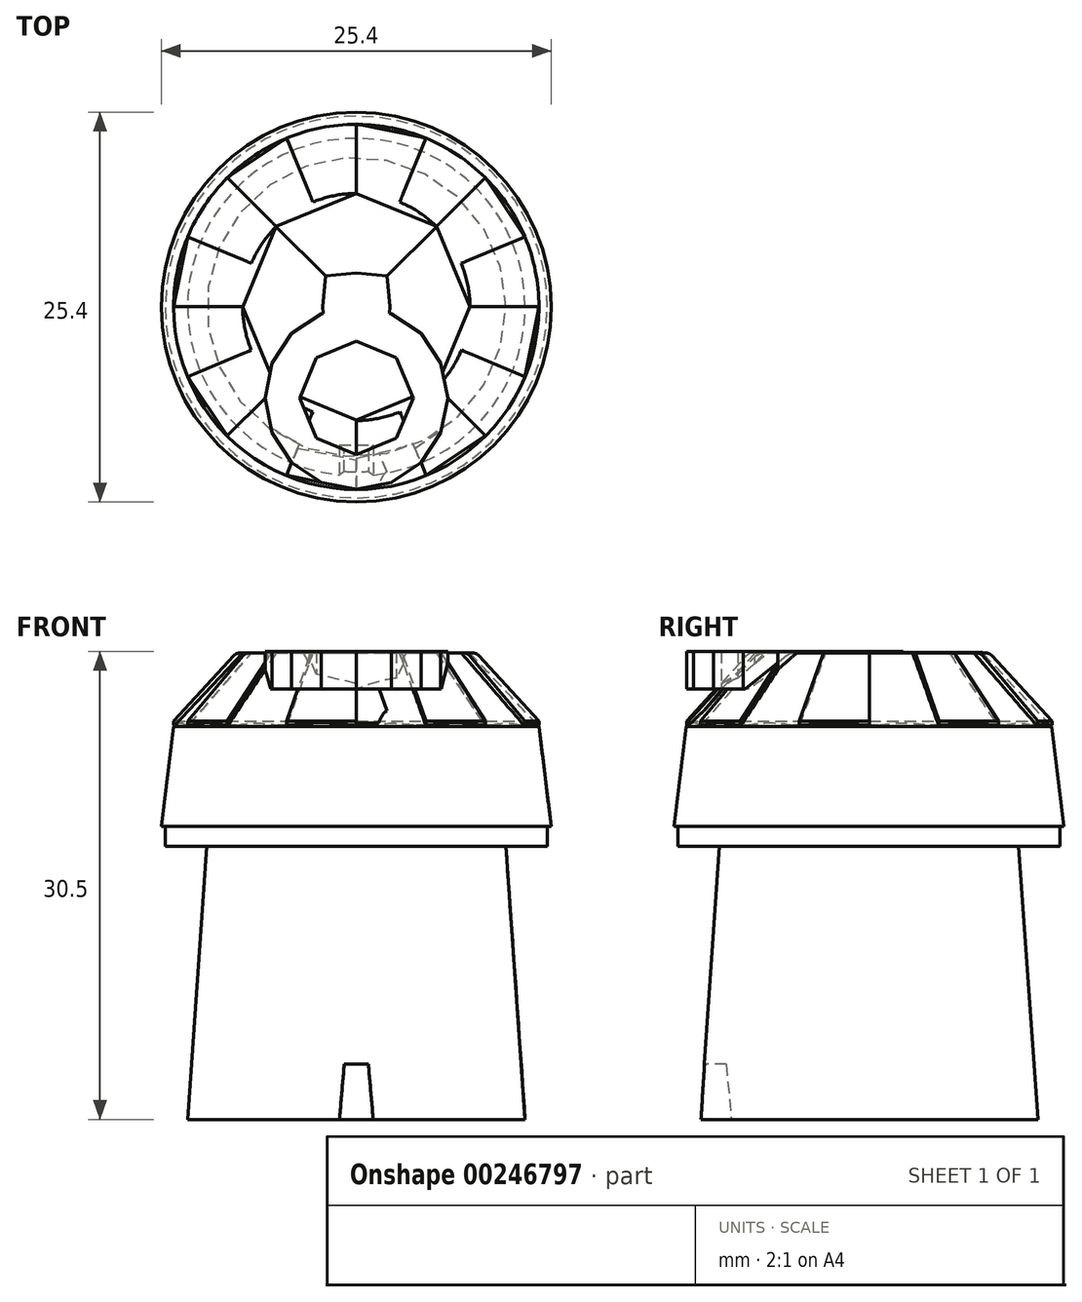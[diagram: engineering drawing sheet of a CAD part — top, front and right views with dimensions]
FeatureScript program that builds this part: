
annotation { "Feature Type Name" : "Feature", "Feature Type Description" : "" }
export const myFeature = defineFeature(function(context is Context, id is Id, definition is map)
    precondition{}
    {
        {
            var Q0;
            Q0=qCreatedBy(makeId("Front.planeOp"),FACE);
            var sketch = newSketch(context, id + "F0", { "sketchPlane" : qUnion([Q0])});
            skLineSegment(sketch, "E0", {"start": v(0, 0) * mm, "end": v(5.5, 0) * mm});
            skLineSegment(sketch, "E1", {"start": v(0, 8.9) * mm, "end": v(4.87, 8.9) * mm});
            skLineSegment(sketch, "E2", {"start": v(4.87, 8.9) * mm, "end": v(5.5, 0) * mm});
            skLineSegment(sketch, "E3", {"start": v(4.87, 8.9) * mm, "end": v(6.22, 8.9) * mm});
            skLineSegment(sketch, "E4", {"start": v(6.22, 8.9) * mm, "end": v(6.22, 9.55) * mm});
            skLineSegment(sketch, "E5", {"start": v(6.22, 9.55) * mm, "end": v(6.35, 9.55) * mm});
            skLineSegment(sketch, "E6", {"start": v(0, 0) * mm, "end": v(0, 15.2) * mm});
            skLineSegment(sketch, "E7", {"start": v(11.32, 12.8) * mm, "end": v(-3.84, 12.8) * mm, "construction": true});
            skLineSegment(sketch, "E8", {"start": v(5.95, 12.8) * mm, "end": v(6.35, 9.55) * mm});
            skLineSegment(sketch, "E9", {"start": v(15.11, 15.2) * mm, "end": v(0, 15.2) * mm, "construction": true});
            skLineSegment(sketch, "E10", {"start": v(0, 15.2) * mm, "end": v(3.7, 15.2) * mm});
            skLineSegment(sketch, "E11", {"start": v(3.7, 15.2) * mm, "end": v(5.95, 12.8) * mm});
            skSolve(sketch);
        }
        {
            var Q0;
            Q0=qSketchRegion(id+"F0",true);
            extrude(context, id + "F1", {"entities" : qUnion([Q0]), "depth" : 0.01 * mm});
        }
        {
            var Q0;
            Q0=makeQuery(id+"F1.opExtrude","CAP_FACE",FACE,{"disambiguationData":[OSD([sQuery(id+"F0.wireOp",EDGE,"E0"),sQuery(id+"F0.wireOp",EDGE,"E2"),sQuery(id+"F0.wireOp",EDGE,"E3"),sQuery(id+"F0.wireOp",EDGE,"E4"),sQuery(id+"F0.wireOp",EDGE,"E5"),sQuery(id+"F0.wireOp",EDGE,"sixM9Us5-RhuG-cWRY-0vQ0-8mJEDSYx7DVo"),sQuery(id+"F0.wireOp",EDGE,"EqexqkoD-ppkq-6j4X-MFRW-SI8jGCcGb6jM"),sQuery(id+"F0.wireOp",EDGE,"g6Ss7R6n-PE6a-QBEk-j47J-OcREIYiym4vq"),sQuery(id+"F0.wireOp",EDGE,"74306cc8-111f-4a76-b4a3-b401b2c3296c0.MirrorCS"),sQuery(id+"F0.wireOp",EDGE,"74306cc8-111f-4a76-b4a3-b401b2c3296c2.MirrorCS"),sQuery(id+"F0.wireOp",EDGE,"74306cc8-111f-4a76-b4a3-b401b2c3296c3.MirrorCS"),sQuery(id+"F0.wireOp",EDGE,"74306cc8-111f-4a76-b4a3-b401b2c3296c6.MirrorCS"),sQuery(id+"F0.wireOp",EDGE,"74306cc8-111f-4a76-b4a3-b401b2c3296c7.MirrorCS"),sQuery(id+"F0.wireOp",EDGE,"74306cc8-111f-4a76-b4a3-b401b2c3296c9.MirrorCS"),sQuery(id+"F0.wireOp",EDGE,"74306cc8-111f-4a76-b4a3-b401b2c3296c13.MirrorCS")])],"isStart":false});
            var Q1;
            Q1=makeQuery(id+"F1.opExtrude","CAP_EDGE",EDGE,{"disambiguationData":[OSD([sQuery(id+"F0.wireOp",EDGE,"E6")])],"isStart":false});
            revolve(context, id + "F2", {"operationType" : NewBodyOperationType.ADD, "entities" : qUnion([Q0]), "axis" : qUnion([Q1]), "revolveType" : RevolveType.FULL});
        }
        {
            var Q0;
            {var subQ0=sQuery(id+"F0.wireOp",EDGE,"E0");Q0=makeQuery(id+"F2.boolean.opBoolean","MERGE",FACE,{"derivedFrom":[makeQuery(id+"F1.opExtrude","SWEPT_FACE",FACE,{"disambiguationData":[OSD([subQ0])]}),makeQuery(id+"F2.opRevolve","SWEPT_FACE",FACE,{"disambiguationData":[OSD([subQ0])]})]});}
            var sketch = newSketch(context, id + "F3", { "sketchPlane" : qUnion([Q0])});
            skCircle(sketch, "E12", {"center": v(0, 0) * mm, "radius": 6 * mm, "construction": true});
            skLineSegment(sketch, "E13", {"start": v(0, 6) * mm, "end": v(0, 4.5) * mm, "construction": true});
            skLineSegment(sketch, "E14", {"start": v(0, 4.5) * mm, "end": v(0.55, 4.5) * mm});
            skLineSegment(sketch, "E15", {"start": v(0.55, 4.5) * mm, "end": v(0.55, 5.97) * mm});
            skLineSegment(sketch, "E16", {"start": v(0, 4.5) * mm, "end": v(-0.55, 4.5) * mm});
            skLineSegment(sketch, "E17", {"start": v(-0.55, 4.5) * mm, "end": v(-0.55, 5.97) * mm});
            skLineSegment(sketch, "E18", {"start": v(-0.55, 5.97) * mm, "end": v(0.55, 5.97) * mm});
            skSolve(sketch);
        }
        {
            var Q0;
            Q0=qSketchRegion(id+"F3",true);
            extrude(context, id + "F4", {"entities" : qUnion([Q0]), "operationType" : NewBodyOperationType.REMOVE, "oppositeDirection" : true, "depth" : 1.8 * mm});
        }
        {
            var Q0;
            Q0=makeQuery(id+"F4.boolean.opBoolean","COPY",EDGE,{"derivedFrom":makeQuery(id+"F4.opExtrude","CAP_EDGE",EDGE,{"disambiguationData":[OSD([sQuery(id+"F3.wireOp",EDGE,"E17")])],"isStart":false})});
            var Q1;
            Q1=makeQuery(id+"F4.boolean.opBoolean","COPY",EDGE,{"derivedFrom":makeQuery(id+"F4.opExtrude","CAP_EDGE",EDGE,{"disambiguationData":[OSD([sQuery(id+"F3.wireOp",EDGE,"E15")])],"isStart":false})});
            var Q2;
            Q2=makeQuery(id+"F4.boolean.opBoolean","COPY",EDGE,{"derivedFrom":makeQuery(id+"F4.opExtrude","CAP_EDGE",EDGE,{"disambiguationData":[OSD([sQuery(id+"F3.wireOp",EDGE,"E14"),sQuery(id+"F3.wireOp",EDGE,"E16")])],"isStart":false})});
            chamfer(context, id + "F5", {"entities" : qUnion([Q0, Q1, Q2]), "chamferType" : ChamferType.OFFSET_ANGLE, "width" : 1.8 * mm, "oppositeDirection" : false, "angle" : 5 * degree, "tangentPropagation" : true});
        }
        {
            var Q0;
            {var subQ0=sQuery(id+"F0.wireOp",EDGE,"E10");Q0=makeQuery(id+"F2.boolean.opBoolean","MERGE",FACE,{"derivedFrom":[makeQuery(id+"F1.opExtrude","SWEPT_FACE",FACE,{"disambiguationData":[OSD([subQ0])]}),makeQuery(id+"F2.opRevolve","SWEPT_FACE",FACE,{"disambiguationData":[OSD([subQ0])]})]});}
            var sketch = newSketch(context, id + "F6", { "sketchPlane" : qUnion([Q0])});
            skLineSegment(sketch, "E19.bottom", {"start": v(1, -1) * mm, "end": v(-1, -1) * mm, "construction": true});
            skLineSegment(sketch, "E19.top", {"start": v(1, 1) * mm, "end": v(-1, 1) * mm, "construction": true});
            skLineSegment(sketch, "E19.left", {"start": v(1, -1) * mm, "end": v(1, 1) * mm, "construction": true});
            skLineSegment(sketch, "E19.right", {"start": v(-1, -1) * mm, "end": v(-1, 1) * mm, "construction": true});
            skPoint(sketch, "E19.middle", {"position": v(0, 0) * mm});
            skLineSegment(sketch, "E20", {"start": v(0, 0) * mm, "end": v(1.1, 0) * mm, "construction": true});
            skPoint(sketch, "E20.endSnap0", {"position": v(1, 0) * mm});
            skLineSegment(sketch, "E21", {"start": v(0, 0) * mm, "end": v(0, 1.1) * mm, "construction": true});
            skPoint(sketch, "E21.endSnap0", {"position": v(0, 1) * mm});
            skLineSegment(sketch, "E22", {"start": v(0, 0) * mm, "end": v(-1.1, 0) * mm, "construction": true});
            skLineSegment(sketch, "E23", {"start": v(0, 0) * mm, "end": v(0, -1.1) * mm, "construction": true});
            skPoint(sketch, "E23.endSnap0", {"position": v(0, -1) * mm});
            skLineSegment(sketch, "E24", {"start": v(1, 1) * mm, "end": v(1.1, 0) * mm});
            skLineSegment(sketch, "E25", {"start": v(1, -1) * mm, "end": v(1.1, 0) * mm});
            skLineSegment(sketch, "E26", {"start": v(0, 1.1) * mm, "end": v(1, 1) * mm});
            skLineSegment(sketch, "E27", {"start": v(0, 1.1) * mm, "end": v(-1, 1) * mm});
            skLineSegment(sketch, "E28", {"start": v(-1, 1) * mm, "end": v(-1.1, 0) * mm});
            skLineSegment(sketch, "E29", {"start": v(-1, -1) * mm, "end": v(-1.1, 0) * mm});
            skLineSegment(sketch, "E30", {"start": v(-1, -1) * mm, "end": v(0, -1.1) * mm});
            skLineSegment(sketch, "E31", {"start": v(1, -1) * mm, "end": v(0, -1.1) * mm});
            skCircle(sketch, "E32", {"center": v(0, 0) * mm, "radius": 3.7 * mm, "construction": true});
            skLineSegment(sketch, "E33", {"start": v(0, -1.1) * mm, "end": v(0, -3.7) * mm, "construction": true});
            skLineSegment(sketch, "E34.bottom", {"start": v(2.62, -2.62) * mm, "end": v(-2.62, -2.62) * mm, "construction": true});
            skLineSegment(sketch, "E34.top", {"start": v(2.62, 2.62) * mm, "end": v(-2.62, 2.62) * mm, "construction": true});
            skLineSegment(sketch, "E34.left", {"start": v(2.62, -2.62) * mm, "end": v(2.62, 2.62) * mm, "construction": true});
            skLineSegment(sketch, "E34.right", {"start": v(-2.62, -2.62) * mm, "end": v(-2.62, 2.62) * mm, "construction": true});
            skLineSegment(sketch, "E35", {"start": v(-2.62, 2.62) * mm, "end": v(-1, 1) * mm});
            skLineSegment(sketch, "E36", {"start": v(-1, -1) * mm, "end": v(-2.62, -2.62) * mm});
            skLineSegment(sketch, "E37", {"start": v(1, -1) * mm, "end": v(2.62, -2.62) * mm});
            skLineSegment(sketch, "E38", {"start": v(1, 1) * mm, "end": v(2.62, 2.62) * mm});
            skLineSegment(sketch, "E39", {"start": v(-2.62, 2.62) * mm, "end": v(0, 3.69) * mm});
            skLineSegment(sketch, "E40", {"start": v(0, 3.69) * mm, "end": v(2.62, 2.62) * mm});
            skLineSegment(sketch, "E41", {"start": v(2.62, 2.62) * mm, "end": v(3.7, 0) * mm});
            skLineSegment(sketch, "E42", {"start": v(3.7, 0) * mm, "end": v(2.62, -2.62) * mm});
            skLineSegment(sketch, "E43", {"start": v(2.62, -2.62) * mm, "end": v(0, -3.7) * mm});
            skLineSegment(sketch, "E44", {"start": v(-2.62, -2.62) * mm, "end": v(0, -3.7) * mm});
            skLineSegment(sketch, "E45", {"start": v(-2.62, -2.62) * mm, "end": v(-3.7, 0) * mm});
            skLineSegment(sketch, "E46", {"start": v(-3.7, 0) * mm, "end": v(-2.62, 2.62) * mm});
            skSolve(sketch);
        }
        {
            var Q0;
            Q0=makeQuery(id+"F6.imprint","IMPRINT",FACE,{"disambiguationData":[TD([[makeQuery(id+"F6.imprint","IMPRINT",EDGE,{"derivedFrom":sQuery(id+"F6.wireOp",EDGE,"E24")}),-1.0]])]});
            extrude(context, id + "F7", {"entities" : qUnion([Q0]), "operationType" : NewBodyOperationType.ADD, "depth" : 0.05 * mm});
        }
        {
            var Q0;
            {var subQ1=sQuery(id+"F6.wireOp",EDGE,"E28");Q0=makeQuery(id+"F6.imprint","IMPRINT",FACE,{"disambiguationData":[TD([[makeQuery(id+"F6.imprint","IMPRINT",EDGE,{"derivedFrom":subQ1}),-1.0]])]});}
            var Q1;
            {var subQ1=sQuery(id+"F6.wireOp",EDGE,"E24");Q1=makeQuery(id+"F6.imprint","IMPRINT",FACE,{"disambiguationData":[TD([[makeQuery(id+"F6.imprint","IMPRINT",EDGE,{"derivedFrom":subQ1}),1.0]])]});}
            extrude(context, id + "F8", {"entities" : qUnion([Q0, Q1]), "operationType" : NewBodyOperationType.ADD, "depth" : 0.01 * mm});
        }
        {
            var Q0;
            Q0=makeQuery(id+"F6.imprint","IMPRINT",FACE,{"disambiguationData":[TD([[makeQuery(id+"F6.imprint","IMPRINT",EDGE,{"derivedFrom":sQuery(id+"F6.wireOp",EDGE,"E30")}),-1.0]])]});
            var Q1;
            {var subQ5=sQuery(id+"F6.wireOp",EDGE,"E26");Q1=makeQuery(id+"F6.imprint","IMPRINT",FACE,{"disambiguationData":[TD([[makeQuery(id+"F6.imprint","IMPRINT",EDGE,{"derivedFrom":subQ5}),1.0]])]});}
            extrude(context, id + "F9", {"entities" : qUnion([Q0, Q1]), "operationType" : NewBodyOperationType.ADD, "depth" : 0.02 * mm});
        }
        {
            var Q0;
            Q0=qCreatedBy(makeId("Top.planeOp"),FACE);
            cPlane(context, id + "F10", {"entities" : qUnion([Q0]), "cplaneType" : CPlaneType.OFFSET, "offset" : 15.2 * mm, "width" : 150 * mm, "height" : 150 * mm});
        }
        {
            var Q0;
            Q0=qCreatedBy(id+"F10.planeOp",FACE);
            var sketch = newSketch(context, id + "F11", { "sketchPlane" : qUnion([Q0])});
            skLineSegment(sketch, "E47", {"start": v(0, -5.95) * mm, "end": v(0, -3.7) * mm});
            skLineSegment(sketch, "E48", {"start": v(1.3, -3.16) * mm, "end": v(2.28, -5.5) * mm});
            skLineSegment(sketch, "E49.1.0", {"start": v(4.2, -4.2) * mm, "end": v(2.62, -2.62) * mm});
            skLineSegment(sketch, "E49.1.1", {"start": v(3.16, -1.3) * mm, "end": v(5.5, -2.28) * mm});
            skLineSegment(sketch, "E49.2.0", {"start": v(5.95, 0) * mm, "end": v(3.7, 0) * mm});
            skLineSegment(sketch, "E49.2.1", {"start": v(3.16, 1.3) * mm, "end": v(5.5, 2.28) * mm});
            skPoint(sketch, "E49.center", {"position": v(0, 0) * mm});
            skLineSegment(sketch, "E50.1.3.0", {"start": v(4.2, 4.2) * mm, "end": v(2.62, 2.62) * mm});
            skLineSegment(sketch, "E50.3.3.0", {"start": v(1.3, 3.16) * mm, "end": v(2.28, 5.5) * mm});
            skLineSegment(sketch, "E50.1.4.0", {"start": v(0, 5.95) * mm, "end": v(0, 3.7) * mm});
            skLineSegment(sketch, "E50.3.4.0", {"start": v(-1.3, 3.16) * mm, "end": v(-2.28, 5.5) * mm});
            skLineSegment(sketch, "E50.1.5.0", {"start": v(-4.2, 4.2) * mm, "end": v(-2.62, 2.62) * mm});
            skLineSegment(sketch, "E50.3.5.0", {"start": v(-3.16, 1.3) * mm, "end": v(-5.5, 2.28) * mm});
            skLineSegment(sketch, "E50.1.6.0", {"start": v(-5.95, 0) * mm, "end": v(-3.7, 0) * mm});
            skLineSegment(sketch, "E50.3.6.0", {"start": v(-3.16, -1.3) * mm, "end": v(-5.5, -2.28) * mm});
            skLineSegment(sketch, "E50.1.7.0", {"start": v(-4.2, -4.2) * mm, "end": v(-2.62, -2.62) * mm});
            skLineSegment(sketch, "E50.3.7.0", {"start": v(-1.3, -3.16) * mm, "end": v(-2.28, -5.5) * mm});
            skLineSegment(sketch, "E51", {"start": v(0, -3.7) * mm, "end": v(1.3, -3.16) * mm});
            skLineSegment(sketch, "E52", {"start": v(1.3, -3.16) * mm, "end": v(2.62, -2.62) * mm});
            skLineSegment(sketch, "E53", {"start": v(2.62, -2.62) * mm, "end": v(3.16, -1.3) * mm});
            skLineSegment(sketch, "E54", {"start": v(3.16, -1.3) * mm, "end": v(3.7, 0) * mm});
            skLineSegment(sketch, "E55", {"start": v(3.7, 0) * mm, "end": v(3.16, 1.3) * mm});
            skLineSegment(sketch, "E56", {"start": v(3.16, 1.3) * mm, "end": v(2.62, 2.62) * mm});
            skLineSegment(sketch, "E57", {"start": v(2.62, 2.62) * mm, "end": v(1.3, 3.16) * mm});
            skLineSegment(sketch, "E58", {"start": v(1.3, 3.16) * mm, "end": v(0, 3.7) * mm});
            skLineSegment(sketch, "E59", {"start": v(0, 3.7) * mm, "end": v(-1.3, 3.16) * mm});
            skLineSegment(sketch, "E60", {"start": v(-1.3, 3.16) * mm, "end": v(-2.62, 2.62) * mm});
            skLineSegment(sketch, "E61", {"start": v(-2.62, 2.62) * mm, "end": v(-3.16, 1.3) * mm});
            skLineSegment(sketch, "E62", {"start": v(-3.16, 1.3) * mm, "end": v(-3.7, 0) * mm});
            skLineSegment(sketch, "E63", {"start": v(-3.7, 0) * mm, "end": v(-3.16, -1.3) * mm});
            skLineSegment(sketch, "E64", {"start": v(-3.16, -1.3) * mm, "end": v(-2.62, -2.62) * mm});
            skLineSegment(sketch, "E65", {"start": v(-2.62, -2.62) * mm, "end": v(-1.3, -3.16) * mm});
            skLineSegment(sketch, "E66", {"start": v(-1.3, -3.16) * mm, "end": v(0, -3.7) * mm});
            skLineSegment(sketch, "E67", {"start": v(-2.28, -5.5) * mm, "end": v(0, -5.95) * mm});
            skLineSegment(sketch, "E68", {"start": v(0, -5.95) * mm, "end": v(2.28, -5.5) * mm});
            skLineSegment(sketch, "E69", {"start": v(2.28, -5.5) * mm, "end": v(4.2, -4.2) * mm});
            skLineSegment(sketch, "E70", {"start": v(4.2, -4.2) * mm, "end": v(5.5, -2.28) * mm});
            skLineSegment(sketch, "E71", {"start": v(5.5, -2.28) * mm, "end": v(5.95, 0) * mm});
            skLineSegment(sketch, "E72", {"start": v(5.95, 0) * mm, "end": v(5.5, 2.28) * mm});
            skLineSegment(sketch, "E73", {"start": v(5.5, 2.28) * mm, "end": v(4.2, 4.2) * mm});
            skLineSegment(sketch, "E74", {"start": v(4.2, 4.2) * mm, "end": v(2.28, 5.5) * mm});
            skLineSegment(sketch, "E75", {"start": v(2.28, 5.5) * mm, "end": v(0, 5.95) * mm});
            skLineSegment(sketch, "E76", {"start": v(0, 5.95) * mm, "end": v(-2.28, 5.5) * mm});
            skLineSegment(sketch, "E77", {"start": v(-2.28, 5.5) * mm, "end": v(-4.2, 4.2) * mm});
            skLineSegment(sketch, "E78", {"start": v(-4.2, 4.2) * mm, "end": v(-5.5, 2.28) * mm});
            skLineSegment(sketch, "E79", {"start": v(-5.5, 2.28) * mm, "end": v(-5.95, 0) * mm});
            skLineSegment(sketch, "E80", {"start": v(-5.95, 0) * mm, "end": v(-5.5, -2.28) * mm});
            skLineSegment(sketch, "E81", {"start": v(-5.5, -2.28) * mm, "end": v(-4.2, -4.2) * mm});
            skLineSegment(sketch, "E82", {"start": v(-4.2, -4.2) * mm, "end": v(-2.28, -5.5) * mm});
            skSolve(sketch);
        }
        {
            var Q0;
            Q0=makeQuery(id+"F11.imprint","IMPRINT",FACE,{"disambiguationData":[TD([[makeQuery(id+"F11.imprint","IMPRINT",EDGE,{"derivedFrom":sQuery(id+"F11.wireOp",EDGE,"E47")}),1.0]])]});
            var Q1;
            Q1=makeQuery(id+"F11.imprint","IMPRINT",FACE,{"disambiguationData":[TD([[makeQuery(id+"F11.imprint","IMPRINT",EDGE,{"derivedFrom":sQuery(id+"F11.wireOp",EDGE,"E48")}),1.0]])]});
            var Q2;
            Q2=makeQuery(id+"F11.imprint","IMPRINT",FACE,{"disambiguationData":[TD([[makeQuery(id+"F11.imprint","IMPRINT",EDGE,{"derivedFrom":sQuery(id+"F11.wireOp",EDGE,"E49.1.1")}),1.0]])]});
            var Q3;
            Q3=makeQuery(id+"F11.imprint","IMPRINT",FACE,{"disambiguationData":[TD([[makeQuery(id+"F11.imprint","IMPRINT",EDGE,{"derivedFrom":sQuery(id+"F11.wireOp",EDGE,"E49.2.1")}),1.0]])]});
            var Q4;
            Q4=makeQuery(id+"F11.imprint","IMPRINT",FACE,{"disambiguationData":[TD([[makeQuery(id+"F11.imprint","IMPRINT",EDGE,{"derivedFrom":sQuery(id+"F11.wireOp",EDGE,"E50.3.3.0")}),1.0]])]});
            var Q5;
            Q5=makeQuery(id+"F11.imprint","IMPRINT",FACE,{"disambiguationData":[TD([[makeQuery(id+"F11.imprint","IMPRINT",EDGE,{"derivedFrom":sQuery(id+"F11.wireOp",EDGE,"E50.3.4.0")}),1.0]])]});
            var Q6;
            Q6=makeQuery(id+"F11.imprint","IMPRINT",FACE,{"disambiguationData":[TD([[makeQuery(id+"F11.imprint","IMPRINT",EDGE,{"derivedFrom":sQuery(id+"F11.wireOp",EDGE,"E50.3.5.0")}),1.0]])]});
            var Q7;
            Q7=makeQuery(id+"F11.imprint","IMPRINT",FACE,{"disambiguationData":[TD([[makeQuery(id+"F11.imprint","IMPRINT",EDGE,{"derivedFrom":sQuery(id+"F11.wireOp",EDGE,"E50.3.6.0")}),1.0]])]});
            var Q8;
            Q8=makeQuery(id+"F1.opExtrude","SWEPT_BODY",BODY,{"disambiguationData":[OSD([sQuery(id+"F0.wireOp",EDGE,"E0"),sQuery(id+"F0.wireOp",EDGE,"E2"),sQuery(id+"F0.wireOp",EDGE,"E3"),sQuery(id+"F0.wireOp",EDGE,"E4"),sQuery(id+"F0.wireOp",EDGE,"E5"),sQuery(id+"F0.wireOp",EDGE,"E6"),sQuery(id+"F0.wireOp",EDGE,"E8"),sQuery(id+"F0.wireOp",EDGE,"E10"),sQuery(id+"F0.wireOp",EDGE,"E11")])]});
            extrude(context, id + "F12", {"entities" : qUnion([Q0, Q1, Q2, Q3, Q4, Q5, Q6, Q7]), "operationType" : NewBodyOperationType.ADD, "oppositeDirection" : true, "endBoundEntityBody" : qUnion([Q8]), "depth" : 2.35 * mm});
        }
        {
            var Q0;
            Q0=makeQuery(id+"F12.opExtrude","CAP_EDGE",EDGE,{"disambiguationData":[OSD([sQuery(id+"F11.wireOp",EDGE,"E67")])],"isStart":true});
            var Q1;
            Q1=makeQuery(id+"F12.opExtrude","CAP_EDGE",EDGE,{"disambiguationData":[OSD([sQuery(id+"F11.wireOp",EDGE,"E69")])],"isStart":true});
            var Q2;
            Q2=makeQuery(id+"F12.opExtrude","CAP_EDGE",EDGE,{"disambiguationData":[OSD([sQuery(id+"F11.wireOp",EDGE,"E71")])],"isStart":true});
            var Q3;
            Q3=makeQuery(id+"F12.opExtrude","CAP_EDGE",EDGE,{"disambiguationData":[OSD([sQuery(id+"F11.wireOp",EDGE,"E73")])],"isStart":true});
            var Q4;
            Q4=makeQuery(id+"F12.opExtrude","CAP_EDGE",EDGE,{"disambiguationData":[OSD([sQuery(id+"F11.wireOp",EDGE,"E75")])],"isStart":true});
            var Q5;
            Q5=makeQuery(id+"F12.opExtrude","CAP_EDGE",EDGE,{"disambiguationData":[OSD([sQuery(id+"F11.wireOp",EDGE,"E77")])],"isStart":true});
            var Q6;
            Q6=makeQuery(id+"F12.opExtrude","CAP_EDGE",EDGE,{"disambiguationData":[OSD([sQuery(id+"F11.wireOp",EDGE,"E79")])],"isStart":true});
            var Q7;
            Q7=makeQuery(id+"F12.opExtrude","CAP_EDGE",EDGE,{"disambiguationData":[OSD([sQuery(id+"F11.wireOp",EDGE,"E81")])],"isStart":true});
            chamfer(context, id + "F13", {"entities" : qUnion([Q0, Q1, Q2, Q3, Q4, Q5, Q6, Q7]), "chamferType" : ChamferType.OFFSET_ANGLE, "width" : 2 * mm, "oppositeDirection" : false, "angle" : 48 * degree, "tangentPropagation" : true});
        }
        {
            var Q0;
            Q0=makeQuery(id+"F11.imprint","IMPRINT",FACE,{"disambiguationData":[TD([[makeQuery(id+"F11.imprint","IMPRINT",EDGE,{"derivedFrom":sQuery(id+"F11.wireOp",EDGE,"E47")}),-1.0]])]});
            var Q1;
            Q1=makeQuery(id+"F11.imprint","IMPRINT",FACE,{"disambiguationData":[TD([[makeQuery(id+"F11.imprint","IMPRINT",EDGE,{"derivedFrom":sQuery(id+"F11.wireOp",EDGE,"E49.1.0")}),-1.0]])]});
            var Q2;
            Q2=makeQuery(id+"F11.imprint","IMPRINT",FACE,{"disambiguationData":[TD([[makeQuery(id+"F11.imprint","IMPRINT",EDGE,{"derivedFrom":sQuery(id+"F11.wireOp",EDGE,"E49.2.0")}),-1.0]])]});
            var Q3;
            Q3=makeQuery(id+"F11.imprint","IMPRINT",FACE,{"disambiguationData":[TD([[makeQuery(id+"F11.imprint","IMPRINT",EDGE,{"derivedFrom":sQuery(id+"F11.wireOp",EDGE,"E50.1.3.0")}),-1.0]])]});
            var Q4;
            Q4=makeQuery(id+"F11.imprint","IMPRINT",FACE,{"disambiguationData":[TD([[makeQuery(id+"F11.imprint","IMPRINT",EDGE,{"derivedFrom":sQuery(id+"F11.wireOp",EDGE,"E50.1.4.0")}),-1.0]])]});
            var Q5;
            Q5=makeQuery(id+"F11.imprint","IMPRINT",FACE,{"disambiguationData":[TD([[makeQuery(id+"F11.imprint","IMPRINT",EDGE,{"derivedFrom":sQuery(id+"F11.wireOp",EDGE,"E50.1.5.0")}),-1.0]])]});
            var Q6;
            Q6=makeQuery(id+"F11.imprint","IMPRINT",FACE,{"disambiguationData":[TD([[makeQuery(id+"F11.imprint","IMPRINT",EDGE,{"derivedFrom":sQuery(id+"F11.wireOp",EDGE,"E50.1.6.0")}),-1.0]])]});
            var Q7;
            Q7=makeQuery(id+"F11.imprint","IMPRINT",FACE,{"disambiguationData":[TD([[makeQuery(id+"F11.imprint","IMPRINT",EDGE,{"derivedFrom":sQuery(id+"F11.wireOp",EDGE,"E50.1.7.0")}),-1.0]])]});
            extrude(context, id + "F14", {"entities" : qUnion([Q0, Q1, Q2, Q3, Q4, Q5, Q6, Q7]), "oppositeDirection" : true, "depth" : 2.45 * mm});
        }
        {
            var Q0;
            Q0=makeQuery(id+"F14.opExtrude","CAP_EDGE",EDGE,{"disambiguationData":[OSD([sQuery(id+"F11.wireOp",EDGE,"E82")])],"isStart":true});
            var Q1;
            Q1=makeQuery(id+"F14.opExtrude","CAP_EDGE",EDGE,{"disambiguationData":[OSD([sQuery(id+"F11.wireOp",EDGE,"E68")])],"isStart":true});
            var Q2;
            Q2=makeQuery(id+"F14.opExtrude","CAP_EDGE",EDGE,{"disambiguationData":[OSD([sQuery(id+"F11.wireOp",EDGE,"E70")])],"isStart":true});
            var Q3;
            Q3=makeQuery(id+"F14.opExtrude","CAP_EDGE",EDGE,{"disambiguationData":[OSD([sQuery(id+"F11.wireOp",EDGE,"E72")])],"isStart":true});
            var Q4;
            Q4=makeQuery(id+"F14.opExtrude","CAP_EDGE",EDGE,{"disambiguationData":[OSD([sQuery(id+"F11.wireOp",EDGE,"E74")])],"isStart":true});
            var Q5;
            Q5=makeQuery(id+"F14.opExtrude","CAP_EDGE",EDGE,{"disambiguationData":[OSD([sQuery(id+"F11.wireOp",EDGE,"E76")])],"isStart":true});
            var Q6;
            Q6=makeQuery(id+"F14.opExtrude","CAP_EDGE",EDGE,{"disambiguationData":[OSD([sQuery(id+"F11.wireOp",EDGE,"E78")])],"isStart":true});
            var Q7;
            Q7=makeQuery(id+"F14.opExtrude","CAP_EDGE",EDGE,{"disambiguationData":[OSD([sQuery(id+"F11.wireOp",EDGE,"E80")])],"isStart":true});
            chamfer(context, id + "F15", {"entities" : qUnion([Q0, Q1, Q2, Q3, Q4, Q5, Q6, Q7]), "chamferType" : ChamferType.OFFSET_ANGLE, "width" : 2 * mm, "oppositeDirection" : false, "angle" : 48 * degree, "tangentPropagation" : true});
        }
        {
            var Q0;
            Q0=makeQuery(id+"F1.opExtrude","SWEPT_BODY",BODY,{"disambiguationData":[OSD([sQuery(id+"F0.wireOp",EDGE,"E0"),sQuery(id+"F0.wireOp",EDGE,"E2"),sQuery(id+"F0.wireOp",EDGE,"E3"),sQuery(id+"F0.wireOp",EDGE,"E4"),sQuery(id+"F0.wireOp",EDGE,"E5"),sQuery(id+"F0.wireOp",EDGE,"E6"),sQuery(id+"F0.wireOp",EDGE,"E8"),sQuery(id+"F0.wireOp",EDGE,"E10"),sQuery(id+"F0.wireOp",EDGE,"E11")])]});
            var Q1;
            Q1=makeQuery(id+"F12.opExtrude","CAP_VERTEX",VERTEX,{"disambiguationData":[OSD([sQuery(id+"F11.wireOp",EDGE,"E47"),sQuery(id+"F11.wireOp",EDGE,"E67"),sQuery(id+"F11.wireOp",EDGE,"E68")])],"isStart":false});
            transform(context, id + "F16", {"entities" : qUnion([Q0]), "transformType" : TransformType.SCALE_UNIFORMLY, "scale" : 2, "scalePoint" : qUnion([Q1]), "makeCopy" : false});
        }
        {
            var Q0;
            {var subQ0=sQuery(id+"F11.wireOp",EDGE,"E79");var subQ1=sQuery(id+"F0.wireOp",EDGE,"E10");var subQ2=makeQuery(id+"F1.opExtrude","SWEPT_FACE",FACE,{"disambiguationData":[OSD([subQ1])]});var subQ3=sQuery(id+"F0.wireOp",EDGE,"E11");var subQ4=makeQuery(id+"F2.opRevolve","SWEPT_FACE",FACE,{"disambiguationData":[OSD([subQ1])]});var subQ5=sQuery(id+"F6.wireOp",EDGE,"E46");var subQ6=makeQuery(id+"F2.opRevolve","SWEPT_EDGE",EDGE,{"disambiguationData":[OSD([subQ1,subQ3])]});Q0=makeQuery(id+"F13.opChamfer","BLEND_EDGE",EDGE,{"blendedFrom":[makeQuery(id+"F12.opExtrude","CAP_EDGE",EDGE,{"disambiguationData":[OSD([subQ0])],"isStart":true}),makeQuery(id+"F12.boolean.opBoolean","MERGE",FACE,{"derivedFrom":[makeQuery(id+"F8.boolean.opBoolean","SPLIT",FACE,{"disambiguationData":[TD([subQ2,subQ4,makeQuery(id+"F2.opRevolve","SWEPT_FACE",FACE,{"disambiguationData":[OSD([subQ3])]}),makeQuery(id+"F8.opExtrude","SWEPT_FACE",FACE,{"disambiguationData":[OSD([sQuery(id+"F6.wireOp",EDGE,"E45")])]}),makeQuery(id+"F8.opExtrude","SWEPT_FACE",FACE,{"disambiguationData":[OSD([subQ5])]}),makeQuery(id+"F8.opExtrude","SWEPT_FACE",FACE,{"disambiguationData":[OSD([subQ1,subQ3]),TDD([makeQuery(id+"F6.imprint","IMPRINT",EDGE,{"disambiguationData":[TD([[makeQuery(id+"F6.imprint","INTERSECT",VERTEX,{"derivedFrom":[subQ6,subQ5]}),1.0]])],"derivedFrom":subQ6})])]})])],"derivedFrom":makeQuery(id+"F2.boolean.opBoolean","MERGE",FACE,{"derivedFrom":[subQ2,subQ4]})}),makeQuery(id+"F12.opExtrude","CAP_FACE",FACE,{"disambiguationData":[OSD([sQuery(id+"F11.wireOp",EDGE,"E50.3.5.0"),sQuery(id+"F11.wireOp",EDGE,"E50.1.6.0"),sQuery(id+"F11.wireOp",EDGE,"E62"),subQ0])],"isStart":true})]})],"blendedInto":[makeQuery(id+"F12.boolean.opBoolean","MERGE",FACE,{"derivedFrom":[makeQuery(id+"F8.boolean.opBoolean","SPLIT",FACE,{"disambiguationData":[TD([subQ2,subQ4,makeQuery(id+"F2.opRevolve","SWEPT_FACE",FACE,{"disambiguationData":[OSD([subQ3])]}),makeQuery(id+"F8.opExtrude","SWEPT_FACE",FACE,{"disambiguationData":[OSD([sQuery(id+"F6.wireOp",EDGE,"E45")])]}),makeQuery(id+"F8.opExtrude","SWEPT_FACE",FACE,{"disambiguationData":[OSD([subQ5])]}),makeQuery(id+"F8.opExtrude","SWEPT_FACE",FACE,{"disambiguationData":[OSD([subQ1,subQ3]),TDD([makeQuery(id+"F6.imprint","IMPRINT",EDGE,{"disambiguationData":[TD([[makeQuery(id+"F6.imprint","INTERSECT",VERTEX,{"derivedFrom":[subQ6,subQ5]}),1.0]])],"derivedFrom":subQ6})])]})])],"derivedFrom":makeQuery(id+"F2.boolean.opBoolean","MERGE",FACE,{"derivedFrom":[subQ2,subQ4]})}),makeQuery(id+"F12.opExtrude","CAP_FACE",FACE,{"disambiguationData":[OSD([sQuery(id+"F11.wireOp",EDGE,"E50.3.5.0"),sQuery(id+"F11.wireOp",EDGE,"E50.1.6.0"),sQuery(id+"F11.wireOp",EDGE,"E62"),subQ0])],"isStart":true})]})]});}
            var Q1;
            {var subQ0=sQuery(id+"F11.wireOp",EDGE,"E77");var subQ1=sQuery(id+"F6.wireOp",EDGE,"E39");var subQ2=sQuery(id+"F0.wireOp",EDGE,"E11");var subQ3=makeQuery(id+"F2.opRevolve","SWEPT_FACE",FACE,{"disambiguationData":[OSD([subQ2])]});var subQ4=sQuery(id+"F0.wireOp",EDGE,"E10");var subQ5=makeQuery(id+"F2.opRevolve","SWEPT_FACE",FACE,{"disambiguationData":[OSD([subQ4])]});var subQ6=makeQuery(id+"F1.opExtrude","SWEPT_FACE",FACE,{"disambiguationData":[OSD([subQ4])]});var subQ7=makeQuery(id+"F2.opRevolve","SWEPT_EDGE",EDGE,{"disambiguationData":[OSD([subQ4,subQ2])]});var subQ8=sQuery(id+"F6.wireOp",EDGE,"E35");var subQ10=sQuery(id+"F6.wireOp",EDGE,"E38");Q1=makeQuery(id+"F13.opChamfer","BLEND_EDGE",EDGE,{"blendedFrom":[makeQuery(id+"F12.opExtrude","CAP_EDGE",EDGE,{"disambiguationData":[OSD([subQ0])],"isStart":true}),makeQuery(id+"F12.boolean.opBoolean","MERGE",FACE,{"derivedFrom":[makeQuery(id+"F9.boolean.opBoolean","SPLIT",FACE,{"disambiguationData":[TD([makeQuery(id+"F9.opExtrude","SWEPT_FACE",FACE,{"disambiguationData":[OSD([subQ4,subQ2]),TDD([makeQuery(id+"F6.imprint","IMPRINT",EDGE,{"disambiguationData":[TD([[makeQuery(id+"F6.imprint","INTERSECT",VERTEX,{"derivedFrom":[subQ7,subQ1]}),-1.0]])],"derivedFrom":subQ7})])]})])],"derivedFrom":makeQuery(id+"F8.boolean.opBoolean","SPLIT",FACE,{"disambiguationData":[TD([subQ3,makeQuery(id+"F7.opExtrude","SWEPT_FACE",FACE,{"disambiguationData":[OSD([sQuery(id+"F6.wireOp",EDGE,"E26")])]}),makeQuery(id+"F7.opExtrude","SWEPT_FACE",FACE,{"disambiguationData":[OSD([sQuery(id+"F6.wireOp",EDGE,"E27")])]}),makeQuery(id+"F8.opExtrude","SWEPT_FACE",FACE,{"disambiguationData":[OSD([subQ8])]}),makeQuery(id+"F8.opExtrude","SWEPT_FACE",FACE,{"disambiguationData":[OSD([subQ10])]}),makeQuery(id+"F8.opExtrude","SWEPT_FACE",FACE,{"disambiguationData":[OSD([subQ4,subQ2]),TDD([makeQuery(id+"F6.imprint","IMPRINT",EDGE,{"disambiguationData":[TD([[makeQuery(id+"F6.imprint","INTERSECT",VERTEX,{"derivedFrom":[subQ7,sQuery(id+"F6.wireOp",EDGE,"E41")]}),-1.0]])],"derivedFrom":subQ7})])]}),makeQuery(id+"F8.opExtrude","SWEPT_FACE",FACE,{"disambiguationData":[OSD([subQ4,subQ2]),TDD([makeQuery(id+"F6.imprint","IMPRINT",EDGE,{"disambiguationData":[TD([[makeQuery(id+"F6.imprint","INTERSECT",VERTEX,{"derivedFrom":[subQ7,sQuery(id+"F6.wireOp",EDGE,"E46")]}),1.0]])],"derivedFrom":subQ7})])]})])],"derivedFrom":makeQuery(id+"F2.boolean.opBoolean","MERGE",FACE,{"derivedFrom":[subQ6,subQ5]})})}),makeQuery(id+"F12.opExtrude","CAP_FACE",FACE,{"disambiguationData":[OSD([sQuery(id+"F11.wireOp",EDGE,"E50.3.4.0"),sQuery(id+"F11.wireOp",EDGE,"E50.1.5.0"),sQuery(id+"F11.wireOp",EDGE,"E60"),subQ0])],"isStart":true})]})],"blendedInto":[makeQuery(id+"F12.boolean.opBoolean","MERGE",FACE,{"derivedFrom":[makeQuery(id+"F9.boolean.opBoolean","SPLIT",FACE,{"disambiguationData":[TD([makeQuery(id+"F9.opExtrude","SWEPT_FACE",FACE,{"disambiguationData":[OSD([subQ4,subQ2]),TDD([makeQuery(id+"F6.imprint","IMPRINT",EDGE,{"disambiguationData":[TD([[makeQuery(id+"F6.imprint","INTERSECT",VERTEX,{"derivedFrom":[subQ7,subQ1]}),-1.0]])],"derivedFrom":subQ7})])]})])],"derivedFrom":makeQuery(id+"F8.boolean.opBoolean","SPLIT",FACE,{"disambiguationData":[TD([subQ3,makeQuery(id+"F7.opExtrude","SWEPT_FACE",FACE,{"disambiguationData":[OSD([sQuery(id+"F6.wireOp",EDGE,"E26")])]}),makeQuery(id+"F7.opExtrude","SWEPT_FACE",FACE,{"disambiguationData":[OSD([sQuery(id+"F6.wireOp",EDGE,"E27")])]}),makeQuery(id+"F8.opExtrude","SWEPT_FACE",FACE,{"disambiguationData":[OSD([subQ8])]}),makeQuery(id+"F8.opExtrude","SWEPT_FACE",FACE,{"disambiguationData":[OSD([subQ10])]}),makeQuery(id+"F8.opExtrude","SWEPT_FACE",FACE,{"disambiguationData":[OSD([subQ4,subQ2]),TDD([makeQuery(id+"F6.imprint","IMPRINT",EDGE,{"disambiguationData":[TD([[makeQuery(id+"F6.imprint","INTERSECT",VERTEX,{"derivedFrom":[subQ7,sQuery(id+"F6.wireOp",EDGE,"E41")]}),-1.0]])],"derivedFrom":subQ7})])]}),makeQuery(id+"F8.opExtrude","SWEPT_FACE",FACE,{"disambiguationData":[OSD([subQ4,subQ2]),TDD([makeQuery(id+"F6.imprint","IMPRINT",EDGE,{"disambiguationData":[TD([[makeQuery(id+"F6.imprint","INTERSECT",VERTEX,{"derivedFrom":[subQ7,sQuery(id+"F6.wireOp",EDGE,"E46")]}),1.0]])],"derivedFrom":subQ7})])]})])],"derivedFrom":makeQuery(id+"F2.boolean.opBoolean","MERGE",FACE,{"derivedFrom":[subQ6,subQ5]})})}),makeQuery(id+"F12.opExtrude","CAP_FACE",FACE,{"disambiguationData":[OSD([sQuery(id+"F11.wireOp",EDGE,"E50.3.4.0"),sQuery(id+"F11.wireOp",EDGE,"E50.1.5.0"),sQuery(id+"F11.wireOp",EDGE,"E60"),subQ0])],"isStart":true})]})]});}
            var Q2;
            {var subQ0=sQuery(id+"F11.wireOp",EDGE,"E75");var subQ1=sQuery(id+"F0.wireOp",EDGE,"E11");var subQ2=makeQuery(id+"F2.opRevolve","SWEPT_FACE",FACE,{"disambiguationData":[OSD([subQ1])]});var subQ3=sQuery(id+"F0.wireOp",EDGE,"E10");var subQ4=makeQuery(id+"F2.opRevolve","SWEPT_FACE",FACE,{"disambiguationData":[OSD([subQ3])]});var subQ5=makeQuery(id+"F1.opExtrude","SWEPT_FACE",FACE,{"disambiguationData":[OSD([subQ3])]});var subQ6=sQuery(id+"F6.wireOp",EDGE,"E40");var subQ7=makeQuery(id+"F2.opRevolve","SWEPT_EDGE",EDGE,{"disambiguationData":[OSD([subQ3,subQ1])]});var subQ8=sQuery(id+"F6.wireOp",EDGE,"E38");var subQ10=sQuery(id+"F6.wireOp",EDGE,"E35");Q2=makeQuery(id+"F13.opChamfer","BLEND_EDGE",EDGE,{"blendedFrom":[makeQuery(id+"F12.opExtrude","CAP_EDGE",EDGE,{"disambiguationData":[OSD([subQ0])],"isStart":true}),makeQuery(id+"F12.boolean.opBoolean","MERGE",FACE,{"derivedFrom":[makeQuery(id+"F9.boolean.opBoolean","SPLIT",FACE,{"disambiguationData":[TD([makeQuery(id+"F9.opExtrude","SWEPT_FACE",FACE,{"disambiguationData":[OSD([subQ3,subQ1]),TDD([makeQuery(id+"F6.imprint","IMPRINT",EDGE,{"disambiguationData":[TD([[makeQuery(id+"F6.imprint","INTERSECT",VERTEX,{"derivedFrom":[subQ7,subQ6]}),1.0]])],"derivedFrom":subQ7})])]})])],"derivedFrom":makeQuery(id+"F8.boolean.opBoolean","SPLIT",FACE,{"disambiguationData":[TD([subQ2,makeQuery(id+"F7.opExtrude","SWEPT_FACE",FACE,{"disambiguationData":[OSD([sQuery(id+"F6.wireOp",EDGE,"E26")])]}),makeQuery(id+"F7.opExtrude","SWEPT_FACE",FACE,{"disambiguationData":[OSD([sQuery(id+"F6.wireOp",EDGE,"E27")])]}),makeQuery(id+"F8.opExtrude","SWEPT_FACE",FACE,{"disambiguationData":[OSD([subQ10])]}),makeQuery(id+"F8.opExtrude","SWEPT_FACE",FACE,{"disambiguationData":[OSD([subQ8])]}),makeQuery(id+"F8.opExtrude","SWEPT_FACE",FACE,{"disambiguationData":[OSD([subQ3,subQ1]),TDD([makeQuery(id+"F6.imprint","IMPRINT",EDGE,{"disambiguationData":[TD([[makeQuery(id+"F6.imprint","INTERSECT",VERTEX,{"derivedFrom":[subQ7,sQuery(id+"F6.wireOp",EDGE,"E41")]}),-1.0]])],"derivedFrom":subQ7})])]}),makeQuery(id+"F8.opExtrude","SWEPT_FACE",FACE,{"disambiguationData":[OSD([subQ3,subQ1]),TDD([makeQuery(id+"F6.imprint","IMPRINT",EDGE,{"disambiguationData":[TD([[makeQuery(id+"F6.imprint","INTERSECT",VERTEX,{"derivedFrom":[subQ7,sQuery(id+"F6.wireOp",EDGE,"E46")]}),1.0]])],"derivedFrom":subQ7})])]})])],"derivedFrom":makeQuery(id+"F2.boolean.opBoolean","MERGE",FACE,{"derivedFrom":[subQ5,subQ4]})})}),makeQuery(id+"F12.opExtrude","CAP_FACE",FACE,{"disambiguationData":[OSD([sQuery(id+"F11.wireOp",EDGE,"E50.3.3.0"),sQuery(id+"F11.wireOp",EDGE,"E50.1.4.0"),sQuery(id+"F11.wireOp",EDGE,"E58"),subQ0])],"isStart":true})]})],"blendedInto":[makeQuery(id+"F12.boolean.opBoolean","MERGE",FACE,{"derivedFrom":[makeQuery(id+"F9.boolean.opBoolean","SPLIT",FACE,{"disambiguationData":[TD([makeQuery(id+"F9.opExtrude","SWEPT_FACE",FACE,{"disambiguationData":[OSD([subQ3,subQ1]),TDD([makeQuery(id+"F6.imprint","IMPRINT",EDGE,{"disambiguationData":[TD([[makeQuery(id+"F6.imprint","INTERSECT",VERTEX,{"derivedFrom":[subQ7,subQ6]}),1.0]])],"derivedFrom":subQ7})])]})])],"derivedFrom":makeQuery(id+"F8.boolean.opBoolean","SPLIT",FACE,{"disambiguationData":[TD([subQ2,makeQuery(id+"F7.opExtrude","SWEPT_FACE",FACE,{"disambiguationData":[OSD([sQuery(id+"F6.wireOp",EDGE,"E26")])]}),makeQuery(id+"F7.opExtrude","SWEPT_FACE",FACE,{"disambiguationData":[OSD([sQuery(id+"F6.wireOp",EDGE,"E27")])]}),makeQuery(id+"F8.opExtrude","SWEPT_FACE",FACE,{"disambiguationData":[OSD([subQ10])]}),makeQuery(id+"F8.opExtrude","SWEPT_FACE",FACE,{"disambiguationData":[OSD([subQ8])]}),makeQuery(id+"F8.opExtrude","SWEPT_FACE",FACE,{"disambiguationData":[OSD([subQ3,subQ1]),TDD([makeQuery(id+"F6.imprint","IMPRINT",EDGE,{"disambiguationData":[TD([[makeQuery(id+"F6.imprint","INTERSECT",VERTEX,{"derivedFrom":[subQ7,sQuery(id+"F6.wireOp",EDGE,"E41")]}),-1.0]])],"derivedFrom":subQ7})])]}),makeQuery(id+"F8.opExtrude","SWEPT_FACE",FACE,{"disambiguationData":[OSD([subQ3,subQ1]),TDD([makeQuery(id+"F6.imprint","IMPRINT",EDGE,{"disambiguationData":[TD([[makeQuery(id+"F6.imprint","INTERSECT",VERTEX,{"derivedFrom":[subQ7,sQuery(id+"F6.wireOp",EDGE,"E46")]}),1.0]])],"derivedFrom":subQ7})])]})])],"derivedFrom":makeQuery(id+"F2.boolean.opBoolean","MERGE",FACE,{"derivedFrom":[subQ5,subQ4]})})}),makeQuery(id+"F12.opExtrude","CAP_FACE",FACE,{"disambiguationData":[OSD([sQuery(id+"F11.wireOp",EDGE,"E50.3.3.0"),sQuery(id+"F11.wireOp",EDGE,"E50.1.4.0"),sQuery(id+"F11.wireOp",EDGE,"E58"),subQ0])],"isStart":true})]})]});}
            var Q3;
            {var subQ0=sQuery(id+"F11.wireOp",EDGE,"E73");var subQ1=sQuery(id+"F0.wireOp",EDGE,"E11");var subQ2=sQuery(id+"F0.wireOp",EDGE,"E10");var subQ3=makeQuery(id+"F2.opRevolve","SWEPT_FACE",FACE,{"disambiguationData":[OSD([subQ2])]});var subQ4=makeQuery(id+"F1.opExtrude","SWEPT_FACE",FACE,{"disambiguationData":[OSD([subQ2])]});var subQ5=sQuery(id+"F6.wireOp",EDGE,"E41");var subQ6=makeQuery(id+"F2.opRevolve","SWEPT_EDGE",EDGE,{"disambiguationData":[OSD([subQ2,subQ1])]});Q3=makeQuery(id+"F13.opChamfer","BLEND_EDGE",EDGE,{"blendedFrom":[makeQuery(id+"F12.opExtrude","CAP_EDGE",EDGE,{"disambiguationData":[OSD([subQ0])],"isStart":true}),makeQuery(id+"F12.boolean.opBoolean","MERGE",FACE,{"derivedFrom":[makeQuery(id+"F8.boolean.opBoolean","SPLIT",FACE,{"disambiguationData":[TD([subQ4,makeQuery(id+"F1.opExtrude","SWEPT_FACE",FACE,{"disambiguationData":[OSD([subQ1])]}),subQ3,makeQuery(id+"F2.opRevolve","SWEPT_FACE",FACE,{"disambiguationData":[OSD([subQ1])]}),makeQuery(id+"F8.opExtrude","SWEPT_FACE",FACE,{"disambiguationData":[OSD([subQ5])]}),makeQuery(id+"F8.opExtrude","SWEPT_FACE",FACE,{"disambiguationData":[OSD([sQuery(id+"F6.wireOp",EDGE,"E42")])]}),makeQuery(id+"F8.opExtrude","SWEPT_FACE",FACE,{"disambiguationData":[OSD([subQ2,subQ1]),TDD([makeQuery(id+"F6.imprint","IMPRINT",EDGE,{"disambiguationData":[TD([[makeQuery(id+"F6.imprint","INTERSECT",VERTEX,{"derivedFrom":[subQ6,subQ5]}),-1.0]])],"derivedFrom":subQ6})])]})])],"derivedFrom":makeQuery(id+"F2.boolean.opBoolean","MERGE",FACE,{"derivedFrom":[subQ4,subQ3]})}),makeQuery(id+"F12.opExtrude","CAP_FACE",FACE,{"disambiguationData":[OSD([sQuery(id+"F11.wireOp",EDGE,"E49.2.1"),sQuery(id+"F11.wireOp",EDGE,"E50.1.3.0"),sQuery(id+"F11.wireOp",EDGE,"E56"),subQ0])],"isStart":true})]})],"blendedInto":[makeQuery(id+"F12.boolean.opBoolean","MERGE",FACE,{"derivedFrom":[makeQuery(id+"F8.boolean.opBoolean","SPLIT",FACE,{"disambiguationData":[TD([subQ4,makeQuery(id+"F1.opExtrude","SWEPT_FACE",FACE,{"disambiguationData":[OSD([subQ1])]}),subQ3,makeQuery(id+"F2.opRevolve","SWEPT_FACE",FACE,{"disambiguationData":[OSD([subQ1])]}),makeQuery(id+"F8.opExtrude","SWEPT_FACE",FACE,{"disambiguationData":[OSD([subQ5])]}),makeQuery(id+"F8.opExtrude","SWEPT_FACE",FACE,{"disambiguationData":[OSD([sQuery(id+"F6.wireOp",EDGE,"E42")])]}),makeQuery(id+"F8.opExtrude","SWEPT_FACE",FACE,{"disambiguationData":[OSD([subQ2,subQ1]),TDD([makeQuery(id+"F6.imprint","IMPRINT",EDGE,{"disambiguationData":[TD([[makeQuery(id+"F6.imprint","INTERSECT",VERTEX,{"derivedFrom":[subQ6,subQ5]}),-1.0]])],"derivedFrom":subQ6})])]})])],"derivedFrom":makeQuery(id+"F2.boolean.opBoolean","MERGE",FACE,{"derivedFrom":[subQ4,subQ3]})}),makeQuery(id+"F12.opExtrude","CAP_FACE",FACE,{"disambiguationData":[OSD([sQuery(id+"F11.wireOp",EDGE,"E49.2.1"),sQuery(id+"F11.wireOp",EDGE,"E50.1.3.0"),sQuery(id+"F11.wireOp",EDGE,"E56"),subQ0])],"isStart":true})]})]});}
            var Q4;
            {var subQ0=sQuery(id+"F11.wireOp",EDGE,"E71");var subQ1=sQuery(id+"F0.wireOp",EDGE,"E11");var subQ2=sQuery(id+"F0.wireOp",EDGE,"E10");var subQ3=makeQuery(id+"F1.opExtrude","SWEPT_FACE",FACE,{"disambiguationData":[OSD([subQ2])]});var subQ4=makeQuery(id+"F2.opRevolve","SWEPT_FACE",FACE,{"disambiguationData":[OSD([subQ2])]});Q4=makeQuery(id+"F13.opChamfer","BLEND_EDGE",EDGE,{"blendedFrom":[makeQuery(id+"F12.opExtrude","CAP_EDGE",EDGE,{"disambiguationData":[OSD([subQ0])],"isStart":true}),makeQuery(id+"F12.boolean.opBoolean","MERGE",FACE,{"derivedFrom":[makeQuery(id+"F8.boolean.opBoolean","SPLIT",FACE,{"disambiguationData":[TD([subQ3,makeQuery(id+"F1.opExtrude","SWEPT_FACE",FACE,{"disambiguationData":[OSD([subQ1])]}),subQ4,makeQuery(id+"F2.opRevolve","SWEPT_FACE",FACE,{"disambiguationData":[OSD([subQ1])]}),makeQuery(id+"F7.opExtrude","SWEPT_FACE",FACE,{"disambiguationData":[OSD([sQuery(id+"F6.wireOp",EDGE,"E30")])]}),makeQuery(id+"F7.opExtrude","SWEPT_FACE",FACE,{"disambiguationData":[OSD([sQuery(id+"F6.wireOp",EDGE,"E31")])]}),makeQuery(id+"F8.opExtrude","SWEPT_FACE",FACE,{"disambiguationData":[OSD([sQuery(id+"F6.wireOp",EDGE,"E36")])]}),makeQuery(id+"F8.opExtrude","SWEPT_FACE",FACE,{"disambiguationData":[OSD([sQuery(id+"F6.wireOp",EDGE,"E37")])]}),makeQuery(id+"F8.opExtrude","SWEPT_FACE",FACE,{"disambiguationData":[OSD([sQuery(id+"F6.wireOp",EDGE,"E41")])]}),makeQuery(id+"F8.opExtrude","SWEPT_FACE",FACE,{"disambiguationData":[OSD([sQuery(id+"F6.wireOp",EDGE,"E42")])]}),makeQuery(id+"F8.opExtrude","SWEPT_FACE",FACE,{"disambiguationData":[OSD([sQuery(id+"F6.wireOp",EDGE,"E45")])]}),makeQuery(id+"F8.opExtrude","SWEPT_FACE",FACE,{"disambiguationData":[OSD([sQuery(id+"F6.wireOp",EDGE,"E46")])]})])],"derivedFrom":makeQuery(id+"F2.boolean.opBoolean","MERGE",FACE,{"derivedFrom":[subQ3,subQ4]})}),makeQuery(id+"F12.opExtrude","CAP_FACE",FACE,{"disambiguationData":[OSD([sQuery(id+"F11.wireOp",EDGE,"E47"),sQuery(id+"F11.wireOp",EDGE,"E50.3.7.0"),sQuery(id+"F11.wireOp",EDGE,"E66"),sQuery(id+"F11.wireOp",EDGE,"E67")])],"isStart":true}),makeQuery(id+"F12.opExtrude","CAP_FACE",FACE,{"disambiguationData":[OSD([sQuery(id+"F11.wireOp",EDGE,"E48"),sQuery(id+"F11.wireOp",EDGE,"E49.1.0"),sQuery(id+"F11.wireOp",EDGE,"E52"),sQuery(id+"F11.wireOp",EDGE,"E69")])],"isStart":true}),makeQuery(id+"F12.opExtrude","CAP_FACE",FACE,{"disambiguationData":[OSD([sQuery(id+"F11.wireOp",EDGE,"E49.1.1"),sQuery(id+"F11.wireOp",EDGE,"E49.2.0"),sQuery(id+"F11.wireOp",EDGE,"E54"),subQ0])],"isStart":true}),makeQuery(id+"F12.opExtrude","CAP_FACE",FACE,{"disambiguationData":[OSD([sQuery(id+"F11.wireOp",EDGE,"E50.3.6.0"),sQuery(id+"F11.wireOp",EDGE,"E50.1.7.0"),sQuery(id+"F11.wireOp",EDGE,"E64"),sQuery(id+"F11.wireOp",EDGE,"E81")])],"isStart":true})]})],"blendedInto":[makeQuery(id+"F12.boolean.opBoolean","MERGE",FACE,{"derivedFrom":[makeQuery(id+"F8.boolean.opBoolean","SPLIT",FACE,{"disambiguationData":[TD([subQ3,makeQuery(id+"F1.opExtrude","SWEPT_FACE",FACE,{"disambiguationData":[OSD([subQ1])]}),subQ4,makeQuery(id+"F2.opRevolve","SWEPT_FACE",FACE,{"disambiguationData":[OSD([subQ1])]}),makeQuery(id+"F7.opExtrude","SWEPT_FACE",FACE,{"disambiguationData":[OSD([sQuery(id+"F6.wireOp",EDGE,"E30")])]}),makeQuery(id+"F7.opExtrude","SWEPT_FACE",FACE,{"disambiguationData":[OSD([sQuery(id+"F6.wireOp",EDGE,"E31")])]}),makeQuery(id+"F8.opExtrude","SWEPT_FACE",FACE,{"disambiguationData":[OSD([sQuery(id+"F6.wireOp",EDGE,"E36")])]}),makeQuery(id+"F8.opExtrude","SWEPT_FACE",FACE,{"disambiguationData":[OSD([sQuery(id+"F6.wireOp",EDGE,"E37")])]}),makeQuery(id+"F8.opExtrude","SWEPT_FACE",FACE,{"disambiguationData":[OSD([sQuery(id+"F6.wireOp",EDGE,"E41")])]}),makeQuery(id+"F8.opExtrude","SWEPT_FACE",FACE,{"disambiguationData":[OSD([sQuery(id+"F6.wireOp",EDGE,"E42")])]}),makeQuery(id+"F8.opExtrude","SWEPT_FACE",FACE,{"disambiguationData":[OSD([sQuery(id+"F6.wireOp",EDGE,"E45")])]}),makeQuery(id+"F8.opExtrude","SWEPT_FACE",FACE,{"disambiguationData":[OSD([sQuery(id+"F6.wireOp",EDGE,"E46")])]})])],"derivedFrom":makeQuery(id+"F2.boolean.opBoolean","MERGE",FACE,{"derivedFrom":[subQ3,subQ4]})}),makeQuery(id+"F12.opExtrude","CAP_FACE",FACE,{"disambiguationData":[OSD([sQuery(id+"F11.wireOp",EDGE,"E47"),sQuery(id+"F11.wireOp",EDGE,"E50.3.7.0"),sQuery(id+"F11.wireOp",EDGE,"E66"),sQuery(id+"F11.wireOp",EDGE,"E67")])],"isStart":true}),makeQuery(id+"F12.opExtrude","CAP_FACE",FACE,{"disambiguationData":[OSD([sQuery(id+"F11.wireOp",EDGE,"E48"),sQuery(id+"F11.wireOp",EDGE,"E49.1.0"),sQuery(id+"F11.wireOp",EDGE,"E52"),sQuery(id+"F11.wireOp",EDGE,"E69")])],"isStart":true}),makeQuery(id+"F12.opExtrude","CAP_FACE",FACE,{"disambiguationData":[OSD([sQuery(id+"F11.wireOp",EDGE,"E49.1.1"),sQuery(id+"F11.wireOp",EDGE,"E49.2.0"),sQuery(id+"F11.wireOp",EDGE,"E54"),subQ0])],"isStart":true}),makeQuery(id+"F12.opExtrude","CAP_FACE",FACE,{"disambiguationData":[OSD([sQuery(id+"F11.wireOp",EDGE,"E50.3.6.0"),sQuery(id+"F11.wireOp",EDGE,"E50.1.7.0"),sQuery(id+"F11.wireOp",EDGE,"E64"),sQuery(id+"F11.wireOp",EDGE,"E81")])],"isStart":true})]})]});}
            var Q5;
            {var subQ0=sQuery(id+"F11.wireOp",EDGE,"E69");var subQ1=sQuery(id+"F0.wireOp",EDGE,"E11");var subQ2=sQuery(id+"F0.wireOp",EDGE,"E10");var subQ3=makeQuery(id+"F1.opExtrude","SWEPT_FACE",FACE,{"disambiguationData":[OSD([subQ2])]});var subQ4=makeQuery(id+"F2.opRevolve","SWEPT_FACE",FACE,{"disambiguationData":[OSD([subQ2])]});Q5=makeQuery(id+"F13.opChamfer","BLEND_EDGE",EDGE,{"blendedFrom":[makeQuery(id+"F12.opExtrude","CAP_EDGE",EDGE,{"disambiguationData":[OSD([subQ0])],"isStart":true}),makeQuery(id+"F12.boolean.opBoolean","MERGE",FACE,{"derivedFrom":[makeQuery(id+"F8.boolean.opBoolean","SPLIT",FACE,{"disambiguationData":[TD([subQ3,makeQuery(id+"F1.opExtrude","SWEPT_FACE",FACE,{"disambiguationData":[OSD([subQ1])]}),subQ4,makeQuery(id+"F2.opRevolve","SWEPT_FACE",FACE,{"disambiguationData":[OSD([subQ1])]}),makeQuery(id+"F7.opExtrude","SWEPT_FACE",FACE,{"disambiguationData":[OSD([sQuery(id+"F6.wireOp",EDGE,"E30")])]}),makeQuery(id+"F7.opExtrude","SWEPT_FACE",FACE,{"disambiguationData":[OSD([sQuery(id+"F6.wireOp",EDGE,"E31")])]}),makeQuery(id+"F8.opExtrude","SWEPT_FACE",FACE,{"disambiguationData":[OSD([sQuery(id+"F6.wireOp",EDGE,"E36")])]}),makeQuery(id+"F8.opExtrude","SWEPT_FACE",FACE,{"disambiguationData":[OSD([sQuery(id+"F6.wireOp",EDGE,"E37")])]}),makeQuery(id+"F8.opExtrude","SWEPT_FACE",FACE,{"disambiguationData":[OSD([sQuery(id+"F6.wireOp",EDGE,"E41")])]}),makeQuery(id+"F8.opExtrude","SWEPT_FACE",FACE,{"disambiguationData":[OSD([sQuery(id+"F6.wireOp",EDGE,"E42")])]}),makeQuery(id+"F8.opExtrude","SWEPT_FACE",FACE,{"disambiguationData":[OSD([sQuery(id+"F6.wireOp",EDGE,"E45")])]}),makeQuery(id+"F8.opExtrude","SWEPT_FACE",FACE,{"disambiguationData":[OSD([sQuery(id+"F6.wireOp",EDGE,"E46")])]})])],"derivedFrom":makeQuery(id+"F2.boolean.opBoolean","MERGE",FACE,{"derivedFrom":[subQ3,subQ4]})}),makeQuery(id+"F12.opExtrude","CAP_FACE",FACE,{"disambiguationData":[OSD([sQuery(id+"F11.wireOp",EDGE,"E47"),sQuery(id+"F11.wireOp",EDGE,"E50.3.7.0"),sQuery(id+"F11.wireOp",EDGE,"E66"),sQuery(id+"F11.wireOp",EDGE,"E67")])],"isStart":true}),makeQuery(id+"F12.opExtrude","CAP_FACE",FACE,{"disambiguationData":[OSD([sQuery(id+"F11.wireOp",EDGE,"E48"),sQuery(id+"F11.wireOp",EDGE,"E49.1.0"),sQuery(id+"F11.wireOp",EDGE,"E52"),subQ0])],"isStart":true}),makeQuery(id+"F12.opExtrude","CAP_FACE",FACE,{"disambiguationData":[OSD([sQuery(id+"F11.wireOp",EDGE,"E49.1.1"),sQuery(id+"F11.wireOp",EDGE,"E49.2.0"),sQuery(id+"F11.wireOp",EDGE,"E54"),sQuery(id+"F11.wireOp",EDGE,"E71")])],"isStart":true}),makeQuery(id+"F12.opExtrude","CAP_FACE",FACE,{"disambiguationData":[OSD([sQuery(id+"F11.wireOp",EDGE,"E50.3.6.0"),sQuery(id+"F11.wireOp",EDGE,"E50.1.7.0"),sQuery(id+"F11.wireOp",EDGE,"E64"),sQuery(id+"F11.wireOp",EDGE,"E81")])],"isStart":true})]})],"blendedInto":[makeQuery(id+"F12.boolean.opBoolean","MERGE",FACE,{"derivedFrom":[makeQuery(id+"F8.boolean.opBoolean","SPLIT",FACE,{"disambiguationData":[TD([subQ3,makeQuery(id+"F1.opExtrude","SWEPT_FACE",FACE,{"disambiguationData":[OSD([subQ1])]}),subQ4,makeQuery(id+"F2.opRevolve","SWEPT_FACE",FACE,{"disambiguationData":[OSD([subQ1])]}),makeQuery(id+"F7.opExtrude","SWEPT_FACE",FACE,{"disambiguationData":[OSD([sQuery(id+"F6.wireOp",EDGE,"E30")])]}),makeQuery(id+"F7.opExtrude","SWEPT_FACE",FACE,{"disambiguationData":[OSD([sQuery(id+"F6.wireOp",EDGE,"E31")])]}),makeQuery(id+"F8.opExtrude","SWEPT_FACE",FACE,{"disambiguationData":[OSD([sQuery(id+"F6.wireOp",EDGE,"E36")])]}),makeQuery(id+"F8.opExtrude","SWEPT_FACE",FACE,{"disambiguationData":[OSD([sQuery(id+"F6.wireOp",EDGE,"E37")])]}),makeQuery(id+"F8.opExtrude","SWEPT_FACE",FACE,{"disambiguationData":[OSD([sQuery(id+"F6.wireOp",EDGE,"E41")])]}),makeQuery(id+"F8.opExtrude","SWEPT_FACE",FACE,{"disambiguationData":[OSD([sQuery(id+"F6.wireOp",EDGE,"E42")])]}),makeQuery(id+"F8.opExtrude","SWEPT_FACE",FACE,{"disambiguationData":[OSD([sQuery(id+"F6.wireOp",EDGE,"E45")])]}),makeQuery(id+"F8.opExtrude","SWEPT_FACE",FACE,{"disambiguationData":[OSD([sQuery(id+"F6.wireOp",EDGE,"E46")])]})])],"derivedFrom":makeQuery(id+"F2.boolean.opBoolean","MERGE",FACE,{"derivedFrom":[subQ3,subQ4]})}),makeQuery(id+"F12.opExtrude","CAP_FACE",FACE,{"disambiguationData":[OSD([sQuery(id+"F11.wireOp",EDGE,"E47"),sQuery(id+"F11.wireOp",EDGE,"E50.3.7.0"),sQuery(id+"F11.wireOp",EDGE,"E66"),sQuery(id+"F11.wireOp",EDGE,"E67")])],"isStart":true}),makeQuery(id+"F12.opExtrude","CAP_FACE",FACE,{"disambiguationData":[OSD([sQuery(id+"F11.wireOp",EDGE,"E48"),sQuery(id+"F11.wireOp",EDGE,"E49.1.0"),sQuery(id+"F11.wireOp",EDGE,"E52"),subQ0])],"isStart":true}),makeQuery(id+"F12.opExtrude","CAP_FACE",FACE,{"disambiguationData":[OSD([sQuery(id+"F11.wireOp",EDGE,"E49.1.1"),sQuery(id+"F11.wireOp",EDGE,"E49.2.0"),sQuery(id+"F11.wireOp",EDGE,"E54"),sQuery(id+"F11.wireOp",EDGE,"E71")])],"isStart":true}),makeQuery(id+"F12.opExtrude","CAP_FACE",FACE,{"disambiguationData":[OSD([sQuery(id+"F11.wireOp",EDGE,"E50.3.6.0"),sQuery(id+"F11.wireOp",EDGE,"E50.1.7.0"),sQuery(id+"F11.wireOp",EDGE,"E64"),sQuery(id+"F11.wireOp",EDGE,"E81")])],"isStart":true})]})]});}
            var Q6;
            {var subQ0=sQuery(id+"F11.wireOp",EDGE,"E67");var subQ1=sQuery(id+"F0.wireOp",EDGE,"E11");var subQ2=sQuery(id+"F0.wireOp",EDGE,"E10");var subQ3=makeQuery(id+"F1.opExtrude","SWEPT_FACE",FACE,{"disambiguationData":[OSD([subQ2])]});var subQ4=makeQuery(id+"F2.opRevolve","SWEPT_FACE",FACE,{"disambiguationData":[OSD([subQ2])]});Q6=makeQuery(id+"F13.opChamfer","BLEND_EDGE",EDGE,{"blendedFrom":[makeQuery(id+"F12.opExtrude","CAP_EDGE",EDGE,{"disambiguationData":[OSD([subQ0])],"isStart":true}),makeQuery(id+"F12.boolean.opBoolean","MERGE",FACE,{"derivedFrom":[makeQuery(id+"F8.boolean.opBoolean","SPLIT",FACE,{"disambiguationData":[TD([subQ3,makeQuery(id+"F1.opExtrude","SWEPT_FACE",FACE,{"disambiguationData":[OSD([subQ1])]}),subQ4,makeQuery(id+"F2.opRevolve","SWEPT_FACE",FACE,{"disambiguationData":[OSD([subQ1])]}),makeQuery(id+"F7.opExtrude","SWEPT_FACE",FACE,{"disambiguationData":[OSD([sQuery(id+"F6.wireOp",EDGE,"E30")])]}),makeQuery(id+"F7.opExtrude","SWEPT_FACE",FACE,{"disambiguationData":[OSD([sQuery(id+"F6.wireOp",EDGE,"E31")])]}),makeQuery(id+"F8.opExtrude","SWEPT_FACE",FACE,{"disambiguationData":[OSD([sQuery(id+"F6.wireOp",EDGE,"E36")])]}),makeQuery(id+"F8.opExtrude","SWEPT_FACE",FACE,{"disambiguationData":[OSD([sQuery(id+"F6.wireOp",EDGE,"E37")])]}),makeQuery(id+"F8.opExtrude","SWEPT_FACE",FACE,{"disambiguationData":[OSD([sQuery(id+"F6.wireOp",EDGE,"E41")])]}),makeQuery(id+"F8.opExtrude","SWEPT_FACE",FACE,{"disambiguationData":[OSD([sQuery(id+"F6.wireOp",EDGE,"E42")])]}),makeQuery(id+"F8.opExtrude","SWEPT_FACE",FACE,{"disambiguationData":[OSD([sQuery(id+"F6.wireOp",EDGE,"E45")])]}),makeQuery(id+"F8.opExtrude","SWEPT_FACE",FACE,{"disambiguationData":[OSD([sQuery(id+"F6.wireOp",EDGE,"E46")])]})])],"derivedFrom":makeQuery(id+"F2.boolean.opBoolean","MERGE",FACE,{"derivedFrom":[subQ3,subQ4]})}),makeQuery(id+"F12.opExtrude","CAP_FACE",FACE,{"disambiguationData":[OSD([sQuery(id+"F11.wireOp",EDGE,"E47"),sQuery(id+"F11.wireOp",EDGE,"E50.3.7.0"),sQuery(id+"F11.wireOp",EDGE,"E66"),subQ0])],"isStart":true}),makeQuery(id+"F12.opExtrude","CAP_FACE",FACE,{"disambiguationData":[OSD([sQuery(id+"F11.wireOp",EDGE,"E48"),sQuery(id+"F11.wireOp",EDGE,"E49.1.0"),sQuery(id+"F11.wireOp",EDGE,"E52"),sQuery(id+"F11.wireOp",EDGE,"E69")])],"isStart":true}),makeQuery(id+"F12.opExtrude","CAP_FACE",FACE,{"disambiguationData":[OSD([sQuery(id+"F11.wireOp",EDGE,"E49.1.1"),sQuery(id+"F11.wireOp",EDGE,"E49.2.0"),sQuery(id+"F11.wireOp",EDGE,"E54"),sQuery(id+"F11.wireOp",EDGE,"E71")])],"isStart":true}),makeQuery(id+"F12.opExtrude","CAP_FACE",FACE,{"disambiguationData":[OSD([sQuery(id+"F11.wireOp",EDGE,"E50.3.6.0"),sQuery(id+"F11.wireOp",EDGE,"E50.1.7.0"),sQuery(id+"F11.wireOp",EDGE,"E64"),sQuery(id+"F11.wireOp",EDGE,"E81")])],"isStart":true})]})],"blendedInto":[makeQuery(id+"F12.boolean.opBoolean","MERGE",FACE,{"derivedFrom":[makeQuery(id+"F8.boolean.opBoolean","SPLIT",FACE,{"disambiguationData":[TD([subQ3,makeQuery(id+"F1.opExtrude","SWEPT_FACE",FACE,{"disambiguationData":[OSD([subQ1])]}),subQ4,makeQuery(id+"F2.opRevolve","SWEPT_FACE",FACE,{"disambiguationData":[OSD([subQ1])]}),makeQuery(id+"F7.opExtrude","SWEPT_FACE",FACE,{"disambiguationData":[OSD([sQuery(id+"F6.wireOp",EDGE,"E30")])]}),makeQuery(id+"F7.opExtrude","SWEPT_FACE",FACE,{"disambiguationData":[OSD([sQuery(id+"F6.wireOp",EDGE,"E31")])]}),makeQuery(id+"F8.opExtrude","SWEPT_FACE",FACE,{"disambiguationData":[OSD([sQuery(id+"F6.wireOp",EDGE,"E36")])]}),makeQuery(id+"F8.opExtrude","SWEPT_FACE",FACE,{"disambiguationData":[OSD([sQuery(id+"F6.wireOp",EDGE,"E37")])]}),makeQuery(id+"F8.opExtrude","SWEPT_FACE",FACE,{"disambiguationData":[OSD([sQuery(id+"F6.wireOp",EDGE,"E41")])]}),makeQuery(id+"F8.opExtrude","SWEPT_FACE",FACE,{"disambiguationData":[OSD([sQuery(id+"F6.wireOp",EDGE,"E42")])]}),makeQuery(id+"F8.opExtrude","SWEPT_FACE",FACE,{"disambiguationData":[OSD([sQuery(id+"F6.wireOp",EDGE,"E45")])]}),makeQuery(id+"F8.opExtrude","SWEPT_FACE",FACE,{"disambiguationData":[OSD([sQuery(id+"F6.wireOp",EDGE,"E46")])]})])],"derivedFrom":makeQuery(id+"F2.boolean.opBoolean","MERGE",FACE,{"derivedFrom":[subQ3,subQ4]})}),makeQuery(id+"F12.opExtrude","CAP_FACE",FACE,{"disambiguationData":[OSD([sQuery(id+"F11.wireOp",EDGE,"E47"),sQuery(id+"F11.wireOp",EDGE,"E50.3.7.0"),sQuery(id+"F11.wireOp",EDGE,"E66"),subQ0])],"isStart":true}),makeQuery(id+"F12.opExtrude","CAP_FACE",FACE,{"disambiguationData":[OSD([sQuery(id+"F11.wireOp",EDGE,"E48"),sQuery(id+"F11.wireOp",EDGE,"E49.1.0"),sQuery(id+"F11.wireOp",EDGE,"E52"),sQuery(id+"F11.wireOp",EDGE,"E69")])],"isStart":true}),makeQuery(id+"F12.opExtrude","CAP_FACE",FACE,{"disambiguationData":[OSD([sQuery(id+"F11.wireOp",EDGE,"E49.1.1"),sQuery(id+"F11.wireOp",EDGE,"E49.2.0"),sQuery(id+"F11.wireOp",EDGE,"E54"),sQuery(id+"F11.wireOp",EDGE,"E71")])],"isStart":true}),makeQuery(id+"F12.opExtrude","CAP_FACE",FACE,{"disambiguationData":[OSD([sQuery(id+"F11.wireOp",EDGE,"E50.3.6.0"),sQuery(id+"F11.wireOp",EDGE,"E50.1.7.0"),sQuery(id+"F11.wireOp",EDGE,"E64"),sQuery(id+"F11.wireOp",EDGE,"E81")])],"isStart":true})]})]});}
            var Q7;
            {var subQ0=sQuery(id+"F11.wireOp",EDGE,"E81");var subQ1=sQuery(id+"F0.wireOp",EDGE,"E11");var subQ2=sQuery(id+"F0.wireOp",EDGE,"E10");var subQ3=makeQuery(id+"F1.opExtrude","SWEPT_FACE",FACE,{"disambiguationData":[OSD([subQ2])]});var subQ4=makeQuery(id+"F2.opRevolve","SWEPT_FACE",FACE,{"disambiguationData":[OSD([subQ2])]});Q7=makeQuery(id+"F13.opChamfer","BLEND_EDGE",EDGE,{"blendedFrom":[makeQuery(id+"F12.opExtrude","CAP_EDGE",EDGE,{"disambiguationData":[OSD([subQ0])],"isStart":true}),makeQuery(id+"F12.boolean.opBoolean","MERGE",FACE,{"derivedFrom":[makeQuery(id+"F8.boolean.opBoolean","SPLIT",FACE,{"disambiguationData":[TD([subQ3,makeQuery(id+"F1.opExtrude","SWEPT_FACE",FACE,{"disambiguationData":[OSD([subQ1])]}),subQ4,makeQuery(id+"F2.opRevolve","SWEPT_FACE",FACE,{"disambiguationData":[OSD([subQ1])]}),makeQuery(id+"F7.opExtrude","SWEPT_FACE",FACE,{"disambiguationData":[OSD([sQuery(id+"F6.wireOp",EDGE,"E30")])]}),makeQuery(id+"F7.opExtrude","SWEPT_FACE",FACE,{"disambiguationData":[OSD([sQuery(id+"F6.wireOp",EDGE,"E31")])]}),makeQuery(id+"F8.opExtrude","SWEPT_FACE",FACE,{"disambiguationData":[OSD([sQuery(id+"F6.wireOp",EDGE,"E36")])]}),makeQuery(id+"F8.opExtrude","SWEPT_FACE",FACE,{"disambiguationData":[OSD([sQuery(id+"F6.wireOp",EDGE,"E37")])]}),makeQuery(id+"F8.opExtrude","SWEPT_FACE",FACE,{"disambiguationData":[OSD([sQuery(id+"F6.wireOp",EDGE,"E41")])]}),makeQuery(id+"F8.opExtrude","SWEPT_FACE",FACE,{"disambiguationData":[OSD([sQuery(id+"F6.wireOp",EDGE,"E42")])]}),makeQuery(id+"F8.opExtrude","SWEPT_FACE",FACE,{"disambiguationData":[OSD([sQuery(id+"F6.wireOp",EDGE,"E45")])]}),makeQuery(id+"F8.opExtrude","SWEPT_FACE",FACE,{"disambiguationData":[OSD([sQuery(id+"F6.wireOp",EDGE,"E46")])]})])],"derivedFrom":makeQuery(id+"F2.boolean.opBoolean","MERGE",FACE,{"derivedFrom":[subQ3,subQ4]})}),makeQuery(id+"F12.opExtrude","CAP_FACE",FACE,{"disambiguationData":[OSD([sQuery(id+"F11.wireOp",EDGE,"E47"),sQuery(id+"F11.wireOp",EDGE,"E50.3.7.0"),sQuery(id+"F11.wireOp",EDGE,"E66"),sQuery(id+"F11.wireOp",EDGE,"E67")])],"isStart":true}),makeQuery(id+"F12.opExtrude","CAP_FACE",FACE,{"disambiguationData":[OSD([sQuery(id+"F11.wireOp",EDGE,"E48"),sQuery(id+"F11.wireOp",EDGE,"E49.1.0"),sQuery(id+"F11.wireOp",EDGE,"E52"),sQuery(id+"F11.wireOp",EDGE,"E69")])],"isStart":true}),makeQuery(id+"F12.opExtrude","CAP_FACE",FACE,{"disambiguationData":[OSD([sQuery(id+"F11.wireOp",EDGE,"E49.1.1"),sQuery(id+"F11.wireOp",EDGE,"E49.2.0"),sQuery(id+"F11.wireOp",EDGE,"E54"),sQuery(id+"F11.wireOp",EDGE,"E71")])],"isStart":true}),makeQuery(id+"F12.opExtrude","CAP_FACE",FACE,{"disambiguationData":[OSD([sQuery(id+"F11.wireOp",EDGE,"E50.3.6.0"),sQuery(id+"F11.wireOp",EDGE,"E50.1.7.0"),sQuery(id+"F11.wireOp",EDGE,"E64"),subQ0])],"isStart":true})]})],"blendedInto":[makeQuery(id+"F12.boolean.opBoolean","MERGE",FACE,{"derivedFrom":[makeQuery(id+"F8.boolean.opBoolean","SPLIT",FACE,{"disambiguationData":[TD([subQ3,makeQuery(id+"F1.opExtrude","SWEPT_FACE",FACE,{"disambiguationData":[OSD([subQ1])]}),subQ4,makeQuery(id+"F2.opRevolve","SWEPT_FACE",FACE,{"disambiguationData":[OSD([subQ1])]}),makeQuery(id+"F7.opExtrude","SWEPT_FACE",FACE,{"disambiguationData":[OSD([sQuery(id+"F6.wireOp",EDGE,"E30")])]}),makeQuery(id+"F7.opExtrude","SWEPT_FACE",FACE,{"disambiguationData":[OSD([sQuery(id+"F6.wireOp",EDGE,"E31")])]}),makeQuery(id+"F8.opExtrude","SWEPT_FACE",FACE,{"disambiguationData":[OSD([sQuery(id+"F6.wireOp",EDGE,"E36")])]}),makeQuery(id+"F8.opExtrude","SWEPT_FACE",FACE,{"disambiguationData":[OSD([sQuery(id+"F6.wireOp",EDGE,"E37")])]}),makeQuery(id+"F8.opExtrude","SWEPT_FACE",FACE,{"disambiguationData":[OSD([sQuery(id+"F6.wireOp",EDGE,"E41")])]}),makeQuery(id+"F8.opExtrude","SWEPT_FACE",FACE,{"disambiguationData":[OSD([sQuery(id+"F6.wireOp",EDGE,"E42")])]}),makeQuery(id+"F8.opExtrude","SWEPT_FACE",FACE,{"disambiguationData":[OSD([sQuery(id+"F6.wireOp",EDGE,"E45")])]}),makeQuery(id+"F8.opExtrude","SWEPT_FACE",FACE,{"disambiguationData":[OSD([sQuery(id+"F6.wireOp",EDGE,"E46")])]})])],"derivedFrom":makeQuery(id+"F2.boolean.opBoolean","MERGE",FACE,{"derivedFrom":[subQ3,subQ4]})}),makeQuery(id+"F12.opExtrude","CAP_FACE",FACE,{"disambiguationData":[OSD([sQuery(id+"F11.wireOp",EDGE,"E47"),sQuery(id+"F11.wireOp",EDGE,"E50.3.7.0"),sQuery(id+"F11.wireOp",EDGE,"E66"),sQuery(id+"F11.wireOp",EDGE,"E67")])],"isStart":true}),makeQuery(id+"F12.opExtrude","CAP_FACE",FACE,{"disambiguationData":[OSD([sQuery(id+"F11.wireOp",EDGE,"E48"),sQuery(id+"F11.wireOp",EDGE,"E49.1.0"),sQuery(id+"F11.wireOp",EDGE,"E52"),sQuery(id+"F11.wireOp",EDGE,"E69")])],"isStart":true}),makeQuery(id+"F12.opExtrude","CAP_FACE",FACE,{"disambiguationData":[OSD([sQuery(id+"F11.wireOp",EDGE,"E49.1.1"),sQuery(id+"F11.wireOp",EDGE,"E49.2.0"),sQuery(id+"F11.wireOp",EDGE,"E54"),sQuery(id+"F11.wireOp",EDGE,"E71")])],"isStart":true}),makeQuery(id+"F12.opExtrude","CAP_FACE",FACE,{"disambiguationData":[OSD([sQuery(id+"F11.wireOp",EDGE,"E50.3.6.0"),sQuery(id+"F11.wireOp",EDGE,"E50.1.7.0"),sQuery(id+"F11.wireOp",EDGE,"E64"),subQ0])],"isStart":true})]})]});}
            fillet(context, id + "F17", {"entities" : qUnion([Q0, Q1, Q2, Q3, Q4, Q5, Q6, Q7]), "radius" : 0.5 * mm, "tangentPropagation" : true, "allowEdgeOverflow" : false});
        }
        {
            var Q0;
            Q0=qSketchRegion(id+"F11",true);
            extrude(context, id + "F18", {"entities" : qUnion([Q0]), "operationType" : NewBodyOperationType.ADD, "depth" : 2.45 * mm});
        }
        {
            var Q0;
            Q0=makeQuery(id+"F8.opExtrude","CAP_EDGE",EDGE,{"disambiguationData":[OSD([sQuery(id+"F6.wireOp",EDGE,"E42")])],"isStart":false});
            cPoint(context, id + "F19", {"entities" : qUnion([Q0]), "parameter" : 0.5});
        }
        {
            var Q0;
            Q0=makeQuery(id+"F1.opExtrude","CAP_VERTEX",VERTEX,{"disambiguationData":[OSD([sQuery(id+"F0.wireOp",EDGE,"E8"),sQuery(id+"F0.wireOp",EDGE,"E11")])],"isStart":false});
            var Q1;
            Q1=qCreatedBy(id+"F19",VERTEX);
            var Q2;
            Q2=makeQuery(id+"F8.opExtrude","CAP_VERTEX",VERTEX,{"disambiguationData":[OSD([sQuery(id+"F0.wireOp",EDGE,"E10"),sQuery(id+"F0.wireOp",EDGE,"E11"),sQuery(id+"F6.wireOp",EDGE,"E41"),sQuery(id+"F6.wireOp",EDGE,"E42")])],"isStart":false});
            cPlane(context, id + "F20", {"entities" : qUnion([Q0, Q1, Q2]), "cplaneType" : CPlaneType.THREE_POINT, "offset" : 25 * mm, "width" : 150 * mm, "height" : 150 * mm});
        }
    });
